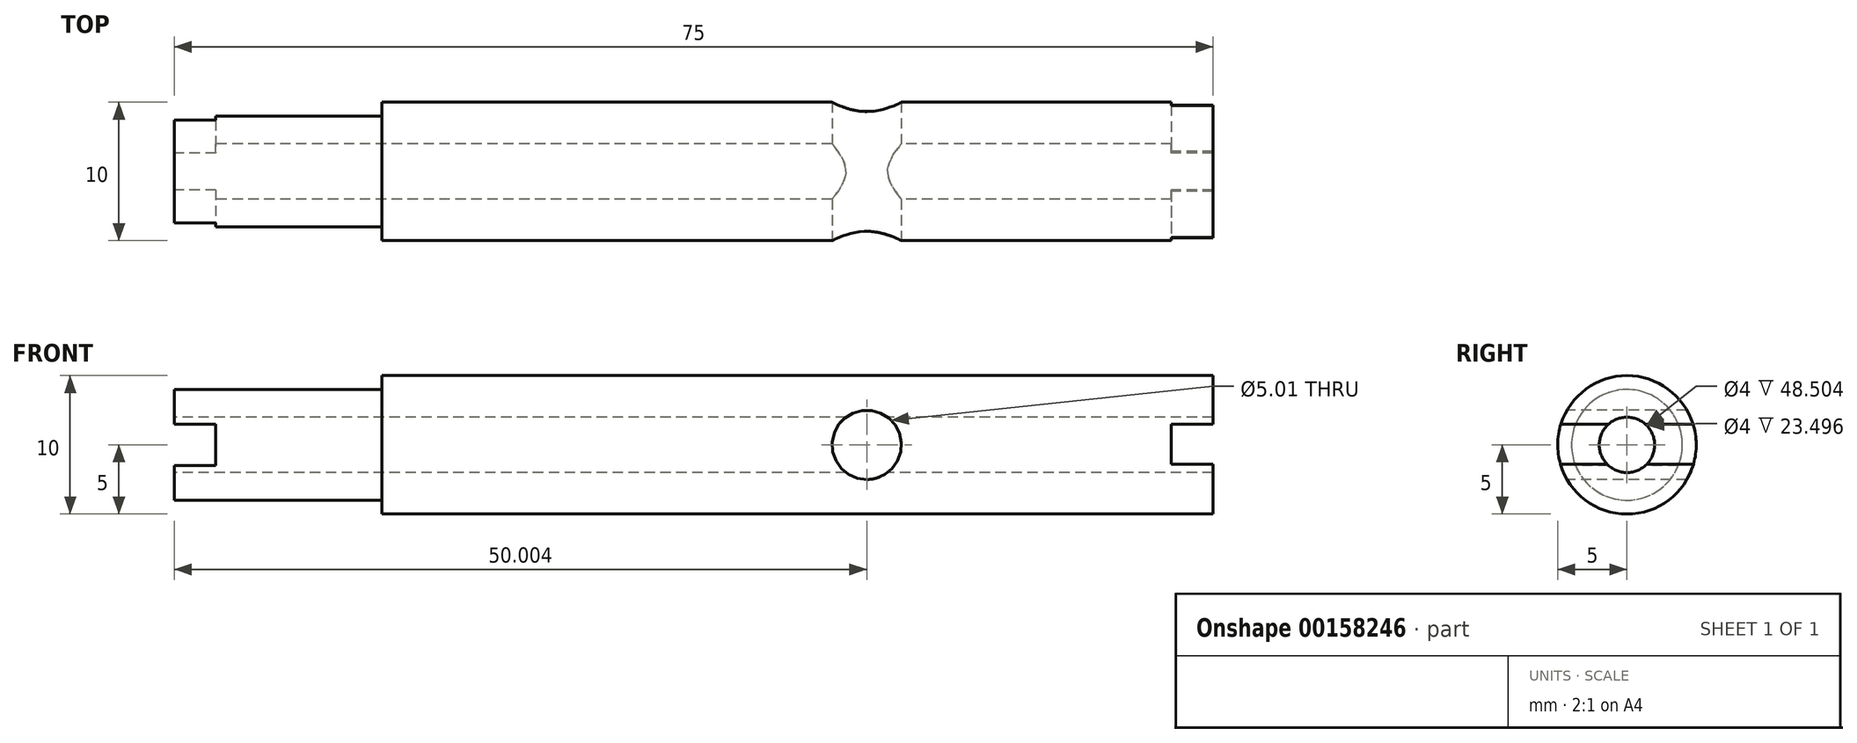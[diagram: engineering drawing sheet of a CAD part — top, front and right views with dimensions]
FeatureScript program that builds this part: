
annotation { "Feature Type Name" : "Feature", "Feature Type Description" : "" }
export const myFeature = defineFeature(function(context is Context, id is Id, definition is map)
    precondition{}
    {
        {
            var Q0;
            Q0=qCreatedBy(makeId("Front.planeOp"),FACE);
            var sketch = newSketch(context, id + "F0", { "sketchPlane" : qUnion([Q0])});
            skLineSegment(sketch, "E0", {"start": v(0, 2) * mm, "end": v(0, 4) * mm});
            skLineSegment(sketch, "E1", {"start": v(0, 4) * mm, "end": v(15, 4) * mm});
            skLineSegment(sketch, "E2", {"start": v(15, 4) * mm, "end": v(15, 5) * mm});
            skLineSegment(sketch, "E3", {"start": v(15, 5) * mm, "end": v(75, 5) * mm});
            skLineSegment(sketch, "E4", {"start": v(75, 5) * mm, "end": v(75, 2) * mm});
            skLineSegment(sketch, "E5", {"start": v(0, 0) * mm, "end": v(75, 0) * mm});
            skLineSegment(sketch, "E6", {"start": v(81.83, 5) * mm, "end": v(81.83, 2) * mm});
            skLineSegment(sketch, "E7", {"start": v(75, 2) * mm, "end": v(0, 2) * mm});
            skSolve(sketch);
        }
        {
            var Q0;
            Q0=makeQuery(id+"F0.imprint","IMPRINT",FACE,{"disambiguationData":[TD([[makeQuery(id+"F0.imprint","IMPRINT",EDGE,{"derivedFrom":sQuery(id+"F0.wireOp",EDGE,"E0")}),-1.0]])]});
            var Q1;
            Q1=sQuery(id+"F0.wireOp",EDGE,"E5");
            revolve(context, id + "F1", {"entities" : qUnion([Q0]), "axis" : qUnion([Q1]), "revolveType" : RevolveType.FULL});
        }
        {
            var Q0;
            Q0=qCreatedBy(makeId("Front.planeOp"),FACE);
            cPlane(context, id + "F2", {"entities" : qUnion([Q0]), "cplaneType" : CPlaneType.OFFSET, "offset" : 10 * mm, "width" : 150 * mm, "height" : 150 * mm});
        }
        {
            var Q0;
            Q0=qCreatedBy(id+"F2.planeOp",FACE);
            var sketch = newSketch(context, id + "F3", { "sketchPlane" : qUnion([Q0])});
            skLineSegment(sketch, "E8", {"start": v(0, 0) * mm, "end": v(0, 1.5) * mm});
            skLineSegment(sketch, "E9", {"start": v(0, 1.5) * mm, "end": v(3, 1.5) * mm});
            skLineSegment(sketch, "E10", {"start": v(3, 1.5) * mm, "end": v(3, -1.5) * mm});
            skLineSegment(sketch, "E11", {"start": v(3, -1.5) * mm, "end": v(0, -1.5) * mm});
            skLineSegment(sketch, "E12", {"start": v(0, -1.5) * mm, "end": v(0, 0) * mm});
            skSolve(sketch);
        }
        {
            var Q0;
            Q0=qCreatedBy(id+"F2.planeOp",FACE);
            var sketch = newSketch(context, id + "F4", { "sketchPlane" : qUnion([Q0])});
            skLineSegment(sketch, "E13.bottom", {"start": v(72, 1.5) * mm, "end": v(75, 1.5) * mm});
            skLineSegment(sketch, "E13.left", {"start": v(72, 1.5) * mm, "end": v(72, 0) * mm});
            skLineSegment(sketch, "E13.right", {"start": v(75, 1.5) * mm, "end": v(75, 0) * mm});
            skLineSegment(sketch, "E14.top", {"start": v(72, -1.38) * mm, "end": v(75, -1.38) * mm});
            skLineSegment(sketch, "E14.left", {"start": v(72, 0) * mm, "end": v(72, -1.38) * mm});
            skLineSegment(sketch, "E14.right", {"start": v(75, 0) * mm, "end": v(75, -1.38) * mm});
            skSolve(sketch);
        }
        {
            var Q0;
            Q0=makeQuery(id+"F4.imprint","IMPRINT",FACE,{"disambiguationData":[TD([[makeQuery(id+"F4.imprint","IMPRINT",EDGE,{"derivedFrom":sQuery(id+"F4.wireOp",EDGE,"E13.bottom")}),-1.0]])]});
            extrude(context, id + "F5", {"entities" : qUnion([Q0]), "operationType" : NewBodyOperationType.REMOVE, "oppositeDirection" : true, "depth" : 25 * mm});
        }
        {
            var Q0;
            Q0=qCreatedBy(makeId("Front.planeOp"),FACE);
            var sketch = newSketch(context, id + "F6", { "sketchPlane" : qUnion([Q0])});
            skLineSegment(sketch, "E15", {"start": v(75, 0) * mm, "end": v(50, 0) * mm});
            skCircle(sketch, "E16", {"center": v(50, 0) * mm, "radius": 2.5 * mm});
            skSolve(sketch);
        }
        {
            var Q0;
            Q0=makeQuery(id+"F6.imprint","IMPRINT",FACE,{"disambiguationData":[TD([[makeQuery(id+"F6.imprint","IMPRINT",EDGE,{"derivedFrom":sQuery(id+"F6.wireOp",EDGE,"E16")}),1.0]])]});
            extrude(context, id + "F7", {"entities" : qUnion([Q0]), "operationType" : NewBodyOperationType.REMOVE, "oppositeDirection" : true, "depth" : 25 * mm, "symmetric" : true});
        }
        {
            var Q0;
            Q0=makeQuery(id+"F3.imprint","IMPRINT",FACE,{"disambiguationData":[TD([[makeQuery(id+"F3.imprint","IMPRINT",EDGE,{"derivedFrom":sQuery(id+"F3.wireOp",EDGE,"E8")}),-1.0]])]});
            extrude(context, id + "F8", {"entities" : qUnion([Q0]), "operationType" : NewBodyOperationType.REMOVE, "oppositeDirection" : true, "depth" : 25 * mm});
        }
    });
